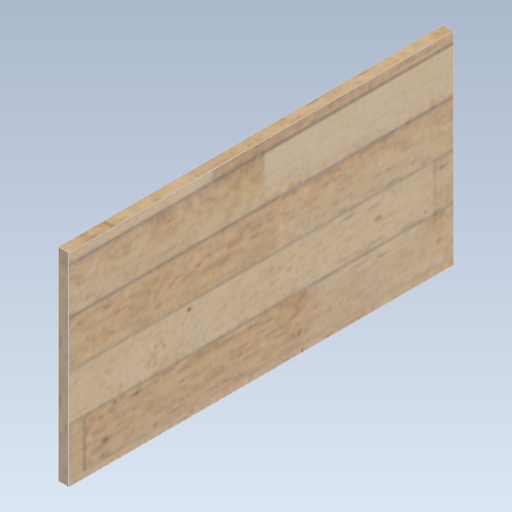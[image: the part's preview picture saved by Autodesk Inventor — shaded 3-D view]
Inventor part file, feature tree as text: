
AUTODESK INVENTOR PART (.ipt)
format: ipt  version: 2021 (Build 250183000, 183)  size: 264,192 bytes
history: native  units: mm
features: extrude x1, sketch x1
ambient origin geometry x8: Origin, YZ Plane, XZ Plane, XY Plane, X Axis, Y Axis, Z Axis, Center Point
bodies: Solid1 (feature_tree)
feature tree (2):
  extrude  "Extrusion1"  [1 undecoded]
  sketch  "Sketch1"  dims[d3=0.0mm]
note: 1 required parameter value undecoded (feature->parameter linkage not recoverable at this tier; creation-order binding heuristic only, values carry confidence <= 0.55)
